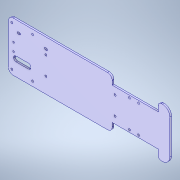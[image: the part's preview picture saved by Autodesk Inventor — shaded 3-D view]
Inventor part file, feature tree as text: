
AUTODESK INVENTOR PART (.ipt)
format: ipt  version: 2020.2 (Build 242310000, 310)  size: 157,184 bytes
history: mixed  units: mm
features: extrude x1, sketch x1, other x1, imported_body x1
ambient origin geometry x8: Origin, YZ Plane, XZ Plane, XY Plane, X Axis, Y Axis, Z Axis, Center Point
bodies: Solide1 (imported_parasolid)
feature tree (4):
  extrude  "Extrusion1"  Depth=3.0mm
  sketch  "Esquisse1"
  other  "PartBody"
  imported_body  NMx_Import_Brep_tag  [imported B-rep: ~52 faces, bbox_mm=[280.0, 86.0, 3.0]]
